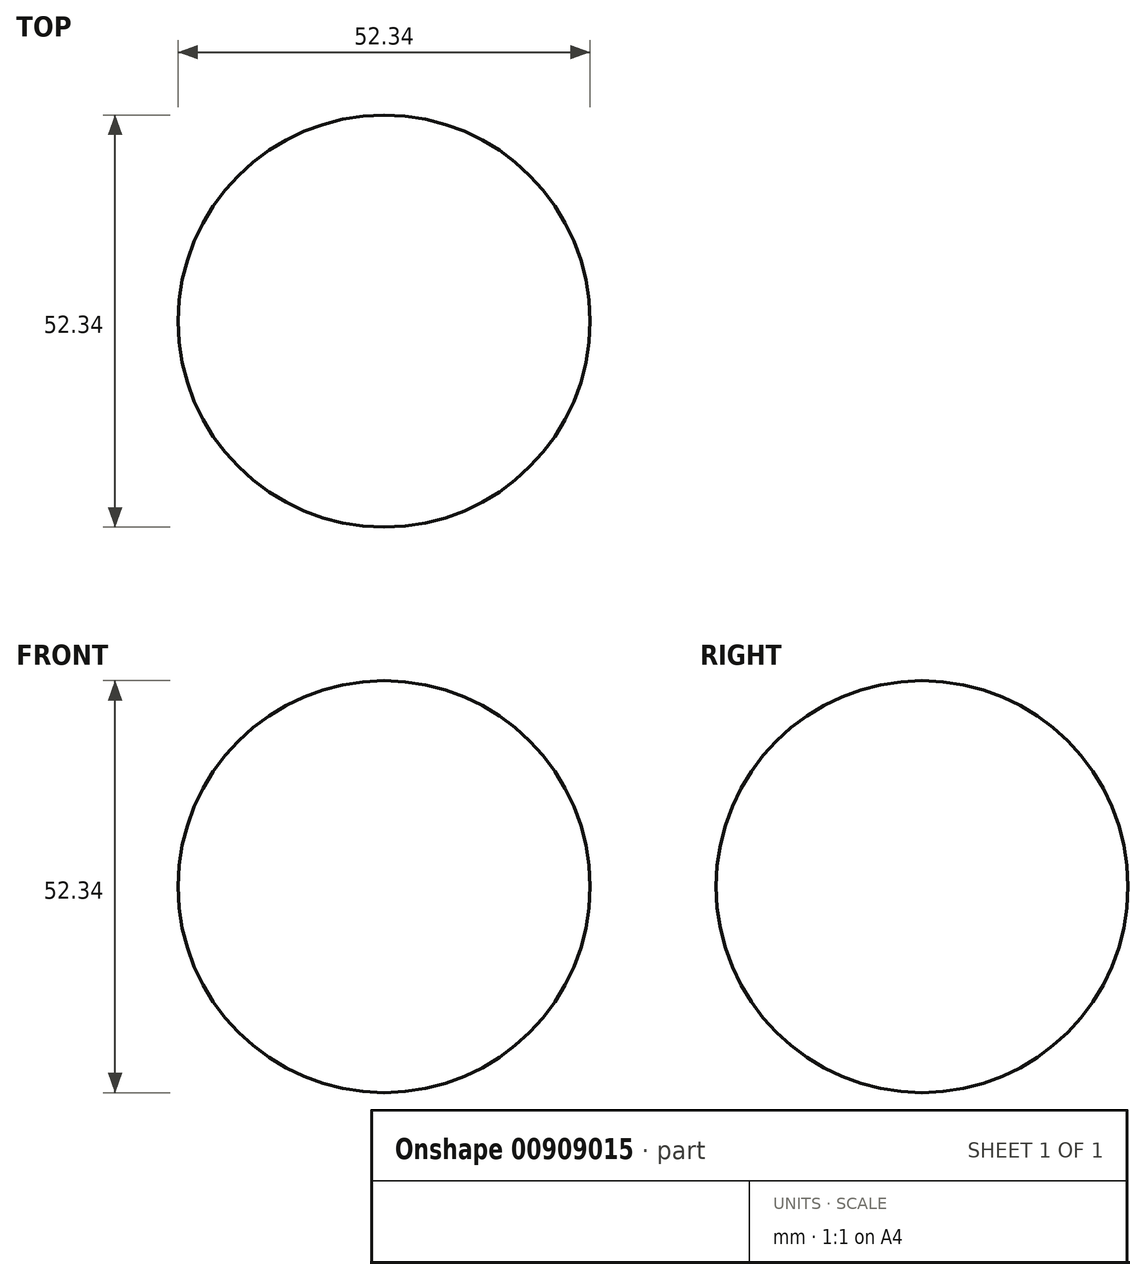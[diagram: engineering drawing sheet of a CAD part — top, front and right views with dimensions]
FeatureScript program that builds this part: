
annotation { "Feature Type Name" : "Feature", "Feature Type Description" : "" }
export const myFeature = defineFeature(function(context is Context, id is Id, definition is map)
    precondition{}
    {
        {
            var Q0;
            Q0=qCreatedBy(makeId("Front.planeOp"),FACE);
            var sketch = newSketch(context, id + "F0", { "sketchPlane" : qUnion([Q0])});
            skArc(sketch, "E0", {"start": v(0, -26.17) * mm, "mid": v(26.17, 0) * mm, "end": v(0, 26.17) * mm});
            skLineSegment(sketch, "E1", {"start": v(0, 26.17) * mm, "end": v(0, -26.17) * mm});
            skSolve(sketch);
        }
        {
            var Q0;
            Q0=makeQuery(id+"F0.imprint","IMPRINT",FACE,{"disambiguationData":[TD([[makeQuery(id+"F0.imprint","IMPRINT",EDGE,{"derivedFrom":sQuery(id+"F0.wireOp",EDGE,"E0")}),1.0]])]});
            var Q1;
            Q1=sQuery(id+"F0.wireOp",EDGE,"E1");
            revolve(context, id + "F1", {"surfaceOperationType" : NewSurfaceOperationType.NEW, "entities" : qUnion([Q0]), "axis" : qUnion([Q1]), "revolveType" : RevolveType.FULL});
        }
    });
